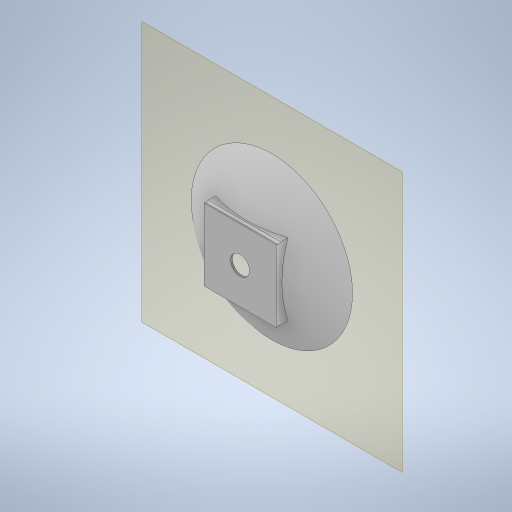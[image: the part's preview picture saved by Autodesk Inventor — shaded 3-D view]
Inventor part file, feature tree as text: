
AUTODESK INVENTOR PART (.ipt)
format: ipt  version: 2023.2 (Build 272271000, 271)  size: 302,592 bytes
history: native  units: mm
features: sketch x5, extrude x4, plane x2, revolve x1, shell x1
ambient origin geometry x8: Origin, YZ Plane, XZ Plane, XY Plane, X Axis, Y Axis, Z Axis, Center Point
bodies: Volumenkörper1 (feature_tree)
feature tree (13):
  revolve  "Umdrehung1"
  plane  "Arbeitsebene1"
  extrude  "Extrusion1"  TaperAngle=360.0deg  [1 undecoded]
  shell  "Wandung1"  Thickness=60.0mm
  plane  "Arbeitsebene2"
  extrude  "Extrusion2"  Depth=0.8mm
  extrude  "Extrusion3"  Depth=50.0mm
  extrude  "Extrusion4"  Depth=10.0mm TaperAngle=0.0deg
  sketch  "Skizze1"  dims[d0=164.0mm d1=360.0deg d2=60.0mm]
  sketch  "Skizze2"  dims[d3=0.0mm d4=0.0mm d5=0.8mm]
  sketch  "Skizze3"  dims[d6=82.0mm d7=50.0mm]
  sketch  "Skizze4"  dims[d8=50.0mm d9=10.0mm d10=0.0mm]
  sketch  "Skizze5"  dims[d12=30.0deg d13=1.5mm d14=0.0mm d15=0.0mm d16=13.0mm d17=0.0mm d18=0.0mm]
note: 1 required parameter value undecoded (feature->parameter linkage not recoverable at this tier; creation-order binding heuristic only, values carry confidence <= 0.55)
